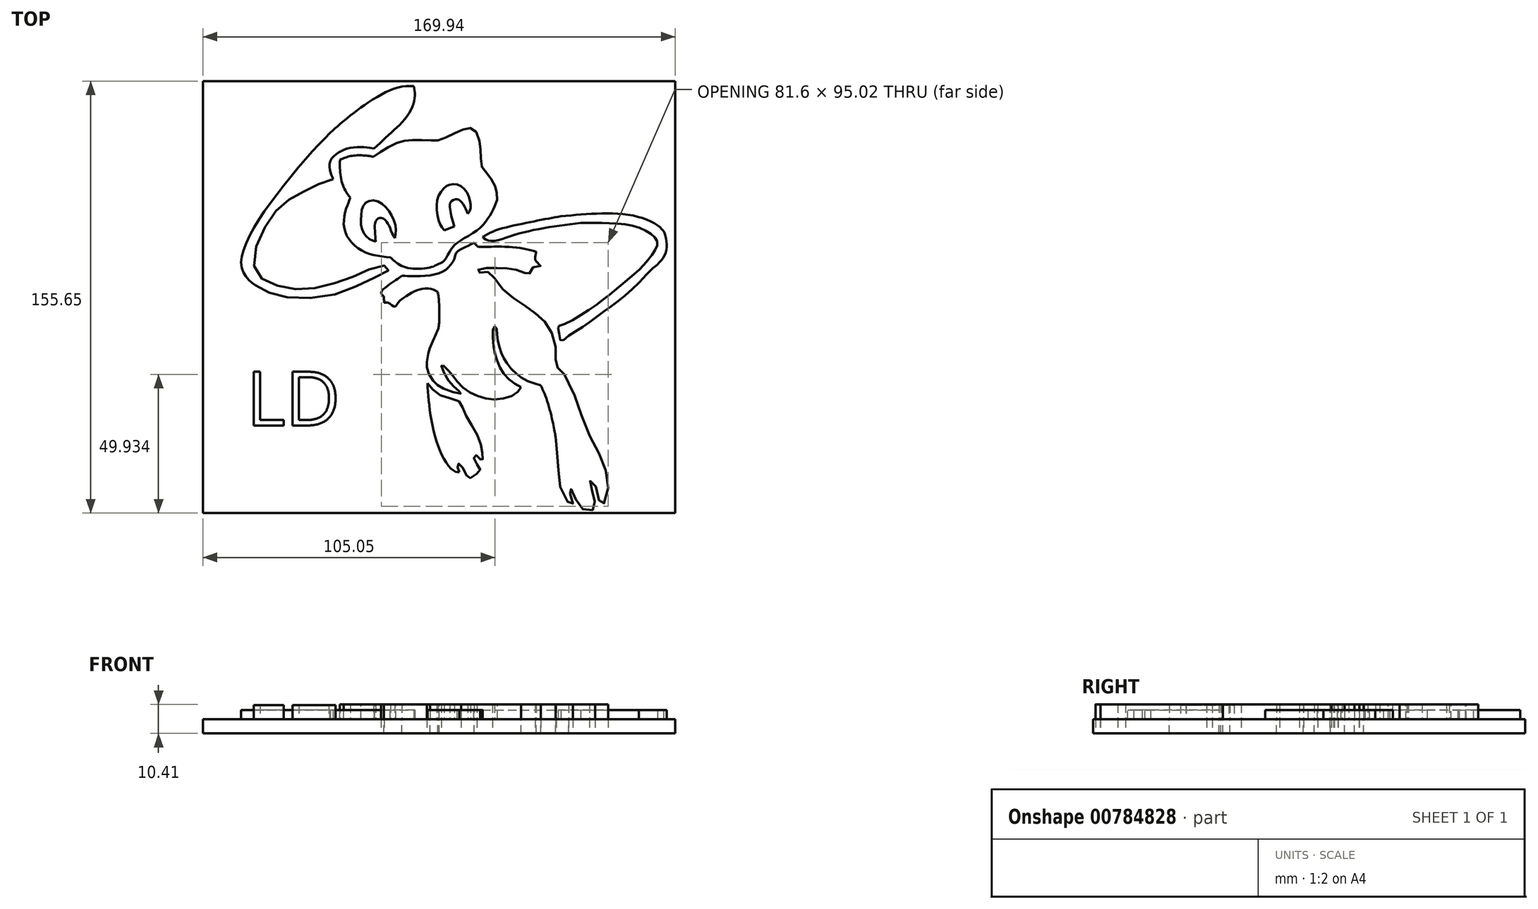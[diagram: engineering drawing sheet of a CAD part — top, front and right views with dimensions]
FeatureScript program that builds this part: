
annotation { "Feature Type Name" : "Feature", "Feature Type Description" : "" }
export const myFeature = defineFeature(function(context is Context, id is Id, definition is map)
    precondition{}
    {
        {
            var Q0;
            Q0=qCreatedBy(makeId("Top.planeOp"),FACE);
            var sketch = newSketch(context, id + "F0", { "sketchPlane" : qUnion([Q0])});
            skFitSpline(sketch, "E0", {"points": [v(-36.88, 36.08) * mm, v(-38.4, 38.25) * mm, v(-40.15, 42.6) * mm, v(-40.65, 48.33) * mm, v(-40.58, 49.85) * mm], "startDerivative": vector(-6.94, 9.09) * mm, "endDerivative": vector(0.6, 7.48) * mm});
            skFitSpline(sketch, "E1", {"points": [v(-40.58, 49.85) * mm, v(-38.04, 50.8) * mm, v(-34.93, 51.37) * mm, v(-31.38, 51.3) * mm, v(-28.55, 50.87) * mm], "startDerivative": vector(10.5, 4.31) * mm, "endDerivative": vector(11.28, -2.04) * mm});
            skFitSpline(sketch, "E2", {"points": [v(-28.55, 50.87) * mm, v(-24.87, 53.3) * mm, v(-19.99, 55.88) * mm, v(-16.36, 56.8) * mm, v(-12.2, 56.87) * mm, v(-6.98, 56.74) * mm, v(-4.41, 57) * mm, v(1, 59.57) * mm, v(4.83, 61.1) * mm, v(7.67, 60.76) * mm, v(9.65, 56.27) * mm, v(10.11, 52.11) * mm, v(10.44, 47.3) * mm, v(11.57, 45.71) * mm, v(14.54, 41.82) * mm, v(15.6, 38.91) * mm, v(16.05, 35.8) * mm, v(15.13, 32.97) * mm], "startDerivative": vector(55.8, 38.5) * mm, "endDerivative": vector(-24.9, -54.1) * mm});
            skFitSpline(sketch, "E3", {"points": [v(15.13, 32.97) * mm, v(13.23, 29.5) * mm, v(9.9, 25.32) * mm, v(3.54, 21.13) * mm, v(0, 18.38) * mm, v(-1.7, 15.62) * mm, v(-3.4, 13.15) * mm, v(-5.2, 12.2) * mm], "startDerivative": vector(-12.69, -24.26) * mm, "endDerivative": vector(-18.67, -6.95) * mm});
            skFitSpline(sketch, "E4", {"points": [v(-5.2, 12.2) * mm, v(-8.38, 10.92) * mm, v(-15.27, 10.68) * mm, v(-19.62, 12.2) * mm, v(-22.36, 14.64) * mm], "startDerivative": vector(-12.64, -6.7) * mm, "endDerivative": vector(-11.41, 11.76) * mm});
            skFitSpline(sketch, "E5", {"points": [v(-22.36, 14.64) * mm, v(-29.1, 15.62) * mm, v(-34.66, 18.38) * mm, v(-38.53, 23.3) * mm, v(-39.1, 28.91) * mm, v(-37.75, 33.9) * mm, v(-36.88, 36.08) * mm], "startDerivative": vector(-36.55, 3.17) * mm, "endDerivative": vector(7.3, 17.53) * mm});
            skFitSpline(sketch, "E6", {"points": [v(-27.74, 20.26) * mm, v(-28, 23.55) * mm, v(-27.97, 26.8) * mm, v(-27.14, 28.47) * mm, v(-25.9, 28.88) * mm, v(-24.15, 27.82) * mm, v(-22.83, 25.7) * mm, v(-21.65, 22.95) * mm, v(-20.94, 21.55) * mm], "startDerivative": vector(-1.85, 21.58) * mm, "endDerivative": vector(6.7, -12.08) * mm});
            skFitSpline(sketch, "E7", {"points": [v(-20.94, 21.55) * mm, v(-20.44, 24.42) * mm, v(-21.43, 28.58) * mm, v(-23.73, 32.29) * mm, v(-27.18, 34.9) * mm, v(-30.4, 34.9) * mm, v(-32.4, 32.97) * mm, v(-32.96, 29.53) * mm, v(-32.93, 25.74) * mm, v(-31.6, 22.72) * mm, v(-29.48, 20.98) * mm, v(-27.74, 20.26) * mm], "startDerivative": vector(8.86, 31.93) * mm, "endDerivative": vector(24.92, -8.61) * mm});
            skLineSegment(sketch, "E8", {"start": v(0.64, 25.77) * mm, "end": v(-3.1, 24.33) * mm});
            skFitSpline(sketch, "E9", {"points": [v(-3.1, 24.33) * mm, v(-4.7, 26.86) * mm, v(-5.73, 31.34) * mm, v(-5.33, 36.17) * mm, v(-3.1, 39.67) * mm, v(-0.97, 40.88) * mm, v(1.96, 40.82) * mm, v(4.95, 38.23) * mm, v(6.27, 34.79) * mm, v(6.39, 32.09) * mm, v(5.4, 30.37) * mm], "startDerivative": vector(-18.53, 24.2) * mm, "endDerivative": vector(-15.72, -20.8) * mm});
            skFitSpline(sketch, "E10", {"points": [v(5.4, 30.37) * mm, v(4.03, 33.3) * mm, v(2.36, 35.3) * mm, v(1.16, 35.6) * mm, v(-0.68, 34.67) * mm, v(-1.02, 32.66) * mm, v(-0.68, 30.37) * mm, v(0, 27.55) * mm, v(0.64, 25.77) * mm], "startDerivative": vector(-8.23, 19.96) * mm, "endDerivative": vector(5.68, -14.34) * mm});
            skFitSpline(sketch, "E11", {"points": [v(-28.3, 53.85) * mm, v(-22.62, 59.17) * mm, v(-17.41, 64.25) * mm, v(-14.15, 69.88) * mm, v(-13.66, 73.45) * mm, v(-13.97, 76.31) * mm], "startDerivative": vector(23.72, 22.62) * mm, "endDerivative": vector(-2.81, 19.35) * mm});
            skFitSpline(sketch, "E12", {"points": [v(-13.97, 76.31) * mm, v(-19.11, 76) * mm, v(-25.25, 73.58) * mm, v(-32.16, 69.26) * mm, v(-37.13, 65.53) * mm, v(-41.53, 61.88) * mm, v(-44.08, 59.5) * mm], "startDerivative": vector(-32.41, 0.3) * mm, "endDerivative": vector(-18.17, -17.44) * mm});
            skFitSpline(sketch, "E13", {"points": [v(-44.08, 59.5) * mm, v(-51.8, 51.48) * mm, v(-63.2, 37.48) * mm, v(-71.34, 25.77) * mm, v(-75.54, 16.64) * mm, v(-76.22, 11.77) * mm, v(-74.95, 8.38) * mm, v(-73.1, 6.15) * mm, v(-70.98, 4.61) * mm], "startDerivative": vector(-48.4, -47.85) * mm, "endDerivative": vector(29.7, -19.4) * mm});
            skFitSpline(sketch, "E14", {"points": [v(-70.98, 4.61) * mm, v(-65.73, 1.76) * mm, v(-56.11, 0) * mm, v(-41.53, 1.5) * mm, v(-30.47, 6.38) * mm, v(-23.8, 9.45) * mm, v(-22.65, 11) * mm, v(-25.86, 11.63) * mm, v(-32.16, 9.32) * mm, v(-40.09, 6.12) * mm, v(-50.09, 3.56) * mm, v(-58.94, 3.43) * mm, v(-66.88, 5.86) * mm, v(-70.98, 9.58) * mm, v(-70.98, 17.91) * mm, v(-66.24, 27.79) * mm, v(-60.86, 34.07) * mm, v(-54.7, 37.79) * mm, v(-48.55, 40.86) * mm, v(-43.04, 42.79) * mm], "startDerivative": vector(103.96, -66.84) * mm, "endDerivative": vector(119.1, 36.89) * mm});
            skFitSpline(sketch, "E15", {"points": [v(-43.04, 42.79) * mm, v(-44.08, 45.32) * mm, v(-44.08, 49.34) * mm, v(-41, 52.5) * mm, v(-36.55, 54.15) * mm, v(-31.3, 54.3) * mm, v(-28.3, 53.85) * mm], "startDerivative": vector(-8.33, 16.7) * mm, "endDerivative": vector(18.9, -3.53) * mm});
            skFitSpline(sketch, "E16", {"points": [v(7.73, 19.96) * mm, v(4.7, 18.38) * mm, v(1.47, 16.59) * mm, v(0.64, 14.22) * mm, v(-1.21, 11.37) * mm, v(-4.34, 9.18) * mm, v(-10.33, 7.93) * mm, v(-15.9, 7.9) * mm, v(-18.3, 8) * mm], "startDerivative": vector(-23.75, -13.65) * mm, "endDerivative": vector(-21.58, 1.02) * mm});
            skFitSpline(sketch, "E17", {"points": [v(-18.3, 8) * mm, v(-21.48, 5.79) * mm, v(-25.73, 2.22) * mm, v(-25.51, 1.24) * mm, v(-24.96, 0.69) * mm, v(-24.75, -0.76) * mm, v(-24.75, -1.78) * mm], "startDerivative": vector(-11.77, -8.3) * mm, "endDerivative": vector(-0.07, -7.72) * mm});
            skFitSpline(sketch, "E18", {"points": [v(-24.75, -1.78) * mm, v(-23.18, -1.78) * mm, v(-20.94, -3.12) * mm, v(-19.7, -1.78) * mm, v(-15.31, 1.57) * mm, v(-11.82, 3.08) * mm, v(-8.28, 3.4) * mm, v(-5.41, 2.2) * mm], "startDerivative": vector(14.29, 3.8) * mm, "endDerivative": vector(18.83, -10.57) * mm});
            skFitSpline(sketch, "E19", {"points": [v(-5.41, -11.46) * mm, v(-6.46, -13.9) * mm, v(-8.5, -18.88) * mm, v(-9.27, -22.77) * mm, v(-9.19, -25.46) * mm, v(-8.23, -28.1) * mm], "startDerivative": vector(-5.21, -12.45) * mm, "endDerivative": vector(6.45, -14.59) * mm});
            skFitSpline(sketch, "E20", {"points": [v(-5.41, -11.46) * mm, v(-5.02, -10.14) * mm, v(-4.86, -5.9) * mm, v(-5.02, -0.37) * mm, v(-5.41, 2.2) * mm], "startDerivative": vector(2.76, 6.94) * mm, "endDerivative": vector(-2.02, 10.26) * mm});
            skFitSpline(sketch, "E21", {"points": [v(-8.23, -28.1) * mm, v(-6.3, -30.62) * mm, v(-2.7, -32.95) * mm, v(3.02, -34.4) * mm, v(1.33, -32.7) * mm, v(-2.6, -28.1) * mm, v(-3.98, -24.1) * mm, v(-2.53, -25.15) * mm, v(0, -28.1) * mm, v(3.82, -32.39) * mm, v(9.45, -35.44) * mm, v(15.89, -36.57) * mm, v(22.56, -34.56) * mm, v(24.65, -32.14) * mm], "startDerivative": vector(28.07, -40.83) * mm, "endDerivative": vector(24.08, 39.06) * mm});
            skFitSpline(sketch, "E22", {"points": [v(24.65, -32.14) * mm, v(19.46, -28.61) * mm, v(16.04, -22.68) * mm, v(14.52, -16.3) * mm, v(14.9, -10.44) * mm, v(15.66, -10.59) * mm, v(15.96, -13.48) * mm, v(17.1, -18.5) * mm, v(18.55, -22.07) * mm, v(21.74, -26.25) * mm, v(26.3, -29.6) * mm, v(31.7, -31.5) * mm], "startDerivative": vector(-53.5, 28.4) * mm, "endDerivative": vector(55.72, -15.9) * mm});
            skFitSpline(sketch, "E23", {"points": [v(31.7, -31.5) * mm, v(33.83, -36.52) * mm, v(35.88, -44.2) * mm, v(36.72, -48.3) * mm, v(37.03, -50.06) * mm], "startDerivative": vector(8, -16.8) * mm, "endDerivative": vector(1.73, -10.31) * mm});
            skFitSpline(sketch, "E24", {"points": [v(37.03, -50.06) * mm, v(37.67, -56.88) * mm, v(38.28, -65.1) * mm, v(40.12, -71.84) * mm, v(43.18, -74.9) * mm, v(43.1, -73.5) * mm, v(42.4, -70.97) * mm, v(41.78, -68.6) * mm, v(42.74, -69.04) * mm, v(44.05, -72.02) * mm, v(46.24, -75.6) * mm, v(48.43, -76.56) * mm, v(50.96, -76.04) * mm, v(51.14, -73.77) * mm, v(50.44, -70) * mm, v(49.3, -67.03) * mm, v(49.65, -65.8) * mm, v(50.96, -67.03) * mm, v(52.28, -70.88) * mm, v(53.41, -74.73) * mm, v(55.25, -72.45) * mm, v(55.69, -64.58) * mm, v(52.89, -56.53) * mm, v(48, -46.82) * mm, v(43.88, -35.1) * mm, v(41.78, -30.72) * mm], "startDerivative": vector(13.24, -128.19) * mm, "endDerivative": vector(-47.37, 85.69) * mm});
            skFitSpline(sketch, "E25", {"points": [v(41.78, -30.72) * mm, v(39.73, -27.08) * mm, v(37.25, -24.41) * mm, v(37.25, -19.83) * mm, v(34.98, -11.16) * mm, v(30.4, -6) * mm, v(23.99, -1.41) * mm, v(17.4, 3.84) * mm, v(13.4, 9.09) * mm, v(11.07, 9.25) * mm, v(8.74, 9.34) * mm, v(9.57, 10.42) * mm, v(12.82, 10.75) * mm, v(17.74, 10.75) * mm, v(21.82, 10.34) * mm, v(25.32, 9.42) * mm, v(27.49, 8.42) * mm, v(27.82, 9.75) * mm, v(29.73, 11.34) * mm, v(31.7, 11.67) * mm, v(30.07, 13.17) * mm], "startDerivative": vector(-32.27, 75.78) * mm, "endDerivative": vector(-69.54, 49.62) * mm});
            skFitSpline(sketch, "E26", {"points": [v(30.07, 13.17) * mm, v(29.68, 13.9) * mm, v(30.07, 16.7) * mm], "startDerivative": vector(-1.4, 1.7) * mm, "endDerivative": vector(1.15, 5.02) * mm});
            skFitSpline(sketch, "E27", {"points": [v(30.07, 16.7) * mm, v(22.73, 18.2) * mm, v(13.95, 18.48) * mm, v(10.79, 18.39) * mm, v(9.05, 18.57) * mm, v(7.73, 19.96) * mm], "startDerivative": vector(-25.6, 6.72) * mm, "endDerivative": vector(-8.87, 12.5) * mm});
            skFitSpline(sketch, "E28", {"points": [v(2.36, -62.8) * mm, v(0.76, -62.5) * mm, v(-2.57, -59) * mm, v(-6.3, -50.06) * mm, v(-8.47, -38.73) * mm, v(-9.1, -30.72) * mm], "startDerivative": vector(-15.3, 0.2) * mm, "endDerivative": vector(-2, 34.43) * mm});
            skFitSpline(sketch, "E29", {"points": [v(-9.1, -30.72) * mm, v(-6.83, -33.36) * mm, v(-2.86, -35.76) * mm, v(1.7, -36.87) * mm, v(3.27, -38.68) * mm, v(4.67, -42.12) * mm, v(7.73, -47.26) * mm, v(9.98, -52.26) * mm, v(10.68, -55.72) * mm, v(10.74, -57.77) * mm, v(10.68, -58.76) * mm, v(9.52, -57.7) * mm, v(8.4, -56.66) * mm, v(7.73, -56.9) * mm, v(7.73, -58) * mm, v(9, -60.22) * mm, v(9.87, -61.8) * mm, v(9.4, -62.79) * mm, v(7, -64.42) * mm, v(5.66, -64.95) * mm, v(4.55, -62.96) * mm, v(3.15, -60.4) * mm, v(2.1, -59.64) * mm, v(1.63, -60.1) * mm, v(1.87, -61.39) * mm, v(2.36, -62.8) * mm], "startDerivative": vector(41.4, -54) * mm, "endDerivative": vector(14.87, -42.66) * mm});
            skFitSpline(sketch, "E30", {"points": [v(10.72, 22.02) * mm, v(15.3, 24.28) * mm, v(23.56, 26.44) * mm, v(32.84, 28.33) * mm, v(38.94, 29.4) * mm], "startDerivative": vector(20, 11.39) * mm, "endDerivative": vector(24.9, 4.23) * mm});
            skFitSpline(sketch, "E31", {"points": [v(10.72, 22.02) * mm, v(12.02, 21) * mm, v(14.93, 20.56) * mm, v(20, 22.02) * mm, v(27.23, 24.07) * mm, v(36.57, 25.8) * mm, v(46, 27.03) * mm], "startDerivative": vector(12.39, -12.48) * mm, "endDerivative": vector(43.26, 5.28) * mm});
            skFitSpline(sketch, "E32", {"points": [v(46, 27.03) * mm, v(54.46, 27.03) * mm, v(64.58, 26.06) * mm, v(71.34, 23.07) * mm, v(73.7, 20) * mm, v(72.38, 16.45) * mm, v(68.06, 11.1) * mm, v(62.98, 6.64) * mm, v(59.01, 3.36) * mm], "startDerivative": vector(56.72, 0.57) * mm, "endDerivative": vector(-34.14, -28.32) * mm});
            skFitSpline(sketch, "E33", {"points": [v(38.94, 29.4) * mm, v(48.57, 30.24) * mm, v(58.73, 30.38) * mm, v(68.13, 28.85) * mm, v(73.84, 26.06) * mm, v(75.93, 24.11) * mm], "startDerivative": vector(41.77, 4.1) * mm, "endDerivative": vector(14.3, -15.48) * mm});
            skFitSpline(sketch, "E34", {"points": [v(59.01, 3.36) * mm, v(52.8, -1.66) * mm, v(46, -6.28) * mm, v(38.94, -9.92) * mm, v(37.93, -10.28) * mm, v(38.17, -12.05) * mm, v(38.94, -15.45) * mm, v(41.63, -13.75) * mm, v(47.58, -9.92) * mm, v(54.08, -5.19) * mm, v(60.39, -0.45) * mm, v(67.07, 5.5) * mm], "startDerivative": vector(-56.72, -47.28) * mm, "endDerivative": vector(57.6, 53.68) * mm});
            skFitSpline(sketch, "E35", {"points": [v(67.07, 5.5) * mm, v(71.5, 10.15) * mm, v(76.76, 16.45) * mm, v(75.93, 24.11) * mm], "startDerivative": vector(12.97, 14.55) * mm, "endDerivative": vector(-7.34, 15.71) * mm});
            skSolve(sketch);
        }
        {
            var Q0;
            Q0=makeQuery(id+"F0.imprint","IMPRINT",FACE,{"disambiguationData":[TD([[makeQuery(id+"F0.imprint","IMPRINT",EDGE,{"derivedFrom":sQuery(id+"F0.wireOp",EDGE,"E0")}),-1.0]])]});
            var Q1;
            Q1=makeQuery(id+"F0.imprint","IMPRINT",FACE,{"disambiguationData":[TD([[makeQuery(id+"F0.imprint","IMPRINT",EDGE,{"derivedFrom":sQuery(id+"F0.wireOp",EDGE,"E16")}),1.0]])]});
            extrude(context, id + "F1", {"entities" : qUnion([Q0, Q1]), "depth" : 5.33 * mm});
        }
        {
            var Q0;
            Q0=makeQuery(id+"F0.imprint","IMPRINT",FACE,{"disambiguationData":[TD([[makeQuery(id+"F0.imprint","IMPRINT",EDGE,{"derivedFrom":sQuery(id+"F0.wireOp",EDGE,"E11")}),1.0]])]});
            var Q1;
            Q1=makeQuery(id+"F0.imprint","IMPRINT",FACE,{"disambiguationData":[TD([[makeQuery(id+"F0.imprint","IMPRINT",EDGE,{"derivedFrom":sQuery(id+"F0.wireOp",EDGE,"E28")}),-1.0]])]});
            var Q2;
            Q2=makeQuery(id+"F0.imprint","IMPRINT",FACE,{"disambiguationData":[TD([[makeQuery(id+"F0.imprint","IMPRINT",EDGE,{"derivedFrom":sQuery(id+"F0.wireOp",EDGE,"E30")}),-1.0]])]});
            extrude(context, id + "F2", {"entities" : qUnion([Q0, Q1, Q2]), "depth" : 3.3 * mm});
        }
        {
            var Q0;
            Q0=makeQuery(id+"F1.opExtrude","CAP_FACE",FACE,{"disambiguationData":[OSD([sQuery(id+"F0.wireOp",EDGE,"E16"),sQuery(id+"F0.wireOp",EDGE,"E17"),sQuery(id+"F0.wireOp",EDGE,"E18"),sQuery(id+"F0.wireOp",EDGE,"E19"),sQuery(id+"F0.wireOp",EDGE,"E20"),sQuery(id+"F0.wireOp",EDGE,"E21"),sQuery(id+"F0.wireOp",EDGE,"E22"),sQuery(id+"F0.wireOp",EDGE,"E23"),sQuery(id+"F0.wireOp",EDGE,"E24"),sQuery(id+"F0.wireOp",EDGE,"E25"),sQuery(id+"F0.wireOp",EDGE,"E26"),sQuery(id+"F0.wireOp",EDGE,"E27")])],"isStart":true});
            var sketch = newSketch(context, id + "F3", { "sketchPlane" : qUnion([Q0])});
            skLineSegment(sketch, "E36.bottom", {"start": v(80.03, 77.48) * mm, "end": v(-89.91, 77.48) * mm});
            skLineSegment(sketch, "E36.top", {"start": v(80.03, -78.17) * mm, "end": v(-89.91, -78.17) * mm});
            skLineSegment(sketch, "E36.left", {"start": v(80.03, 77.48) * mm, "end": v(80.03, -78.17) * mm});
            skLineSegment(sketch, "E36.right", {"start": v(-89.91, 77.48) * mm, "end": v(-89.91, -78.17) * mm});
            skSolve(sketch);
        }
        {
            var Q0;
            Q0=makeQuery(id+"F3.imprint","IMPRINT",FACE,{"disambiguationData":[TD([[makeQuery(id+"F3.imprint","IMPRINT",EDGE,{"derivedFrom":sQuery(id+"F3.wireOp",EDGE,"E36.bottom")}),1.0]])]});
            extrude(context, id + "F4", {"entities" : qUnion([Q0]), "depth" : 5.08 * mm, "offsetDistance" : 25.4 * mm});
        }
        {
            var Q0;
            Q0=makeQuery(id+"F1.opExtrude","CAP_FACE",FACE,{"disambiguationData":[OSD([sQuery(id+"F0.wireOp",EDGE,"E16"),sQuery(id+"F0.wireOp",EDGE,"E17"),sQuery(id+"F0.wireOp",EDGE,"E18"),sQuery(id+"F0.wireOp",EDGE,"E19"),sQuery(id+"F0.wireOp",EDGE,"E20"),sQuery(id+"F0.wireOp",EDGE,"E21"),sQuery(id+"F0.wireOp",EDGE,"E22"),sQuery(id+"F0.wireOp",EDGE,"E23"),sQuery(id+"F0.wireOp",EDGE,"E24"),sQuery(id+"F0.wireOp",EDGE,"E25"),sQuery(id+"F0.wireOp",EDGE,"E26"),sQuery(id+"F0.wireOp",EDGE,"E27")])],"isStart":true});
            extrude(context, id + "F5", {"entities" : qUnion([Q0]), "depth" : 5.08 * mm, "offsetDistance" : 25.4 * mm});
        }
        {
            var Q0;
            Q0=makeQuery(id+"F4.opExtrude","CAP_FACE",FACE,{"disambiguationData":[OSD([sQuery(id+"F0.wireOp",EDGE,"E16"),sQuery(id+"F0.wireOp",EDGE,"E17"),sQuery(id+"F0.wireOp",EDGE,"E18"),sQuery(id+"F0.wireOp",EDGE,"E19"),sQuery(id+"F0.wireOp",EDGE,"E20"),sQuery(id+"F0.wireOp",EDGE,"E21"),sQuery(id+"F0.wireOp",EDGE,"E22"),sQuery(id+"F0.wireOp",EDGE,"E23"),sQuery(id+"F0.wireOp",EDGE,"E24"),sQuery(id+"F0.wireOp",EDGE,"E25"),sQuery(id+"F0.wireOp",EDGE,"E26"),sQuery(id+"F0.wireOp",EDGE,"E27"),sQuery(id+"F3.wireOp",EDGE,"E36.bottom"),sQuery(id+"F3.wireOp",EDGE,"E36.top"),sQuery(id+"F3.wireOp",EDGE,"E36.left"),sQuery(id+"F3.wireOp",EDGE,"E36.right")])],"isStart":true});
            var sketch = newSketch(context, id + "F6", { "sketchPlane" : qUnion([Q0])});
            skText(sketch, "E37", { "text": "LD", "fontName": "OpenSans-Regular.ttf"});
            const initialGuessF6  = {"E37": [-0.07435, -0.04593, 1, 0, 0.0195]};
            skSetInitialGuess(sketch, initialGuessF6);
            skSolve(sketch);
        }
        {
            var Q0;
            Q0 = qSketchRegion(id + "F6", true);
            extrude(context, id + "F7", {"entities" : qUnion([Q0]), "operationType" : NewBodyOperationType.ADD, "depth" : 5.08 * mm, "offsetDistance" : 25.4 * mm});
        }
        {
            var Q0;
            Q0 = qSketchRegion(id + "F6", true);
            extrude(context, id + "F8", {"entities" : qUnion([Q0]), "operationType" : NewBodyOperationType.ADD, "depth" : 2.54 * mm, "offsetDistance" : 25.4 * mm});
        }
    });
